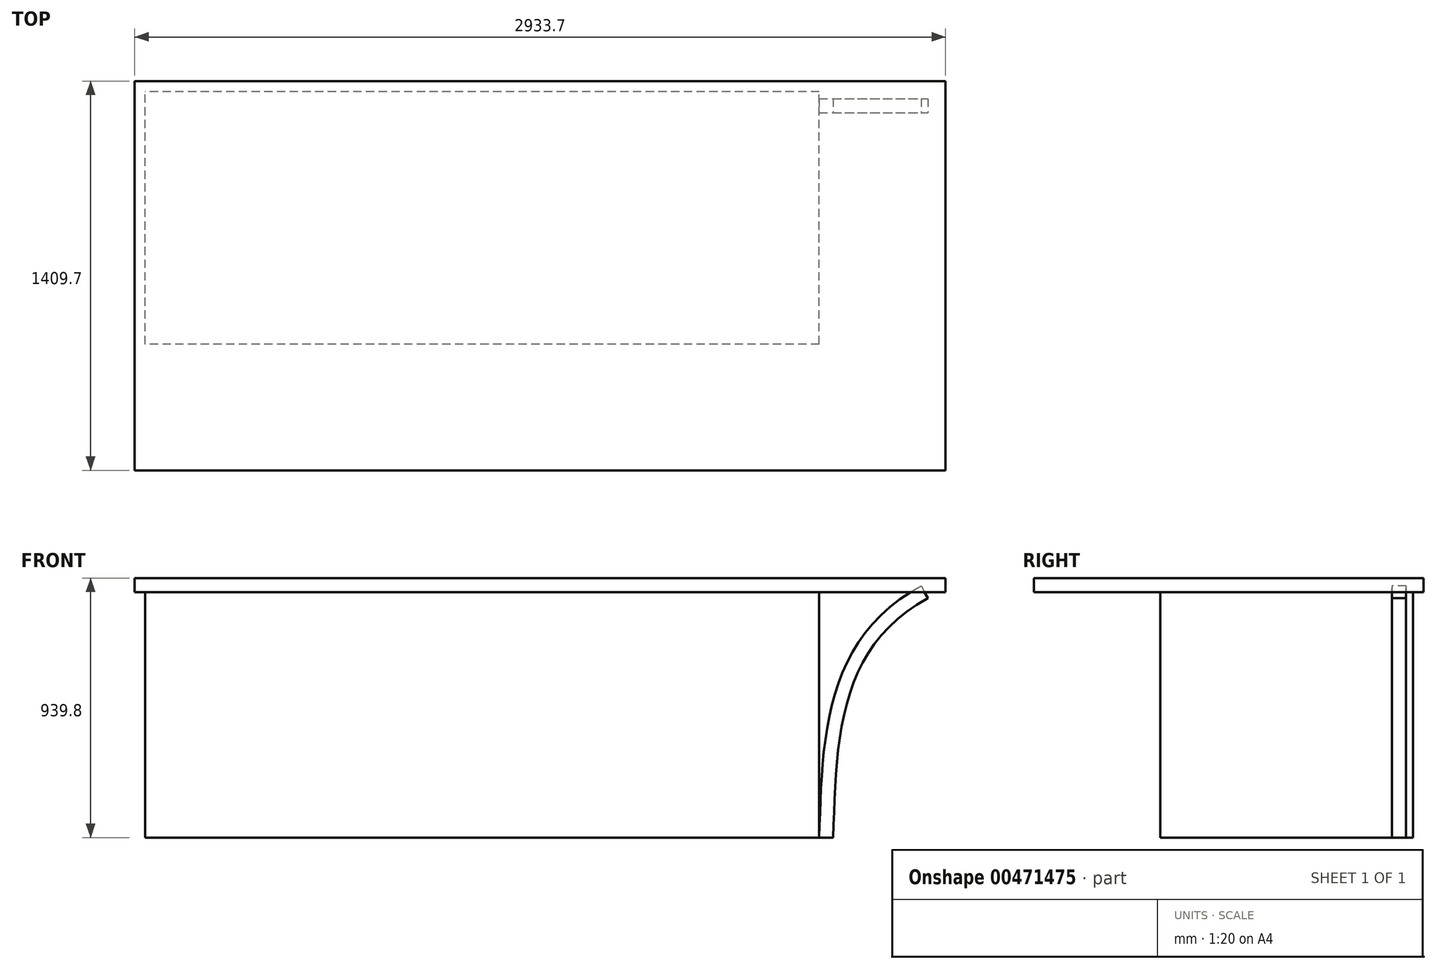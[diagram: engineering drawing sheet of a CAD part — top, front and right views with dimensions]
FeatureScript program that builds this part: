
annotation { "Feature Type Name" : "Feature", "Feature Type Description" : "" }
export const myFeature = defineFeature(function(context is Context, id is Id, definition is map)
    precondition{}
    {
        {
            var Q0;
            Q0=qCreatedBy(makeId("Top.planeOp"),FACE);
            var sketch = newSketch(context, id + "F0", { "sketchPlane" : qUnion([Q0])});
            skLineSegment(sketch, "E0.bottom", {"start": v(1219.2, -460.79) * mm, "end": v(-1219.2, -460.79) * mm});
            skLineSegment(sketch, "E0.top", {"start": v(1219.2, 453.61) * mm, "end": v(-1219.2, 453.61) * mm});
            skLineSegment(sketch, "E0.left", {"start": v(1219.2, -460.79) * mm, "end": v(1219.2, 453.61) * mm});
            skLineSegment(sketch, "E0.right", {"start": v(-1219.2, -460.79) * mm, "end": v(-1219.2, 453.61) * mm});
            skPoint(sketch, "E0.middle", {"position": v(0, -3.59) * mm});
            skSolve(sketch);
        }
        {
            var Q0;
            Q0 = qSketchRegion(id + "F0", true);
            extrude(context, id + "F1", {"entities" : qUnion([Q0]), "depth" : 889 * mm});
        }
        {
            var Q0;
            Q0=makeQuery(id+"F1.opExtrude","CAP_FACE",FACE,{"disambiguationData":[OSD([sQuery(id+"F0.wireOp",EDGE,"E0.bottom"),sQuery(id+"F0.wireOp",EDGE,"E0.top"),sQuery(id+"F0.wireOp",EDGE,"E0.left"),sQuery(id+"F0.wireOp",EDGE,"E0.right")])],"isStart":false});
            var sketch = newSketch(context, id + "F2", { "sketchPlane" : qUnion([Q0])});
            skLineSegment(sketch, "E1.bottom", {"start": v(-1257.3, 491.71) * mm, "end": v(1676.4, 491.71) * mm});
            skLineSegment(sketch, "E1.top", {"start": v(-1257.3, -917.99) * mm, "end": v(1676.4, -917.99) * mm});
            skLineSegment(sketch, "E1.left", {"start": v(-1257.3, 491.71) * mm, "end": v(-1257.3, -917.99) * mm});
            skLineSegment(sketch, "E1.right", {"start": v(1676.4, 491.71) * mm, "end": v(1676.4, -917.99) * mm});
            skSolve(sketch);
        }
        {
            var Q0;
            Q0 = qSketchRegion(id + "F2", true);
            extrude(context, id + "F3", {"entities" : qUnion([Q0]), "depth" : 50.8 * mm});
        }
        {
            var Q0;
            Q0=qCreatedBy(makeId("Top.planeOp"),FACE);
            var sketch = newSketch(context, id + "F4", { "sketchPlane" : qUnion([Q0])});
            skLineSegment(sketch, "E2.bottom", {"start": v(1219.2, 428.21) * mm, "end": v(1270, 428.21) * mm});
            skLineSegment(sketch, "E2.top", {"start": v(1219.2, 377.41) * mm, "end": v(1270, 377.41) * mm});
            skLineSegment(sketch, "E2.left", {"start": v(1219.2, 428.21) * mm, "end": v(1219.2, 377.41) * mm});
            skLineSegment(sketch, "E2.right", {"start": v(1270, 428.21) * mm, "end": v(1270, 377.41) * mm});
            skSolve(sketch);
        }
        {
            var Q0;
            Q0=makeQuery(id+"F3.opExtrude","CAP_FACE",FACE,{"disambiguationData":[OSD([sQuery(id+"F2.wireOp",EDGE,"E1.bottom"),sQuery(id+"F2.wireOp",EDGE,"E1.top"),sQuery(id+"F2.wireOp",EDGE,"E1.left"),sQuery(id+"F2.wireOp",EDGE,"E1.right")])],"isStart":true});
            var sketch = newSketch(context, id + "F5", { "sketchPlane" : qUnion([Q0])});
            skLineSegment(sketch, "E3.bottom", {"start": v(1625.6, -428.21) * mm, "end": v(1574.8, -428.21) * mm});
            skLineSegment(sketch, "E3.top", {"start": v(1625.6, -377.41) * mm, "end": v(1574.8, -377.41) * mm});
            skLineSegment(sketch, "E3.left", {"start": v(1625.6, -428.21) * mm, "end": v(1625.6, -377.41) * mm});
            skLineSegment(sketch, "E3.right", {"start": v(1574.8, -428.21) * mm, "end": v(1574.8, -377.41) * mm});
            skSolve(sketch);
        }
        {
            var Q0;
            Q0=makeQuery(id+"F1.opExtrude","SWEPT_FACE",FACE,{"disambiguationData":[OSD([sQuery(id+"F0.wireOp",EDGE,"E0.top")])]});
            cPlane(context, id + "F6", {"entities" : qUnion([Q0]), "cplaneType" : CPlaneType.OFFSET, "offset" : 50.8 * mm, "oppositeDirection" : true, "width" : 152.4 * mm, "height" : 152.4 * mm});
        }
        {
            var Q0;
            Q0=qCreatedBy(id+"F6.planeOp",FACE);
            var sketch = newSketch(context, id + "F7", { "sketchPlane" : qUnion([Q0])});
            skFitSpline(sketch, "E4", {"points": [v(-1244.6, 0) * mm, v(-1600.2, 889) * mm], "startDerivative": vector(-28.67, 1069.8) * mm, "endDerivative": vector(-1012.7, 547.77) * mm});
            skSolve(sketch);
        }
        {
            var Q0;
            Q0=makeQuery(id+"F4.imprint","IMPRINT",FACE,{"disambiguationData":[TD([[makeQuery(id+"F4.imprint","IMPRINT",EDGE,{"derivedFrom":sQuery(id+"F4.wireOp",EDGE,"E2.bottom")}),-1.0]])]});
            var Q1;
            Q1=sQuery(id+"F7.wireOp",EDGE,"E4");
            sweep(context, id + "F8", {"profiles" : qUnion([Q0]), "path" : qUnion([Q1])});
        }
    });
